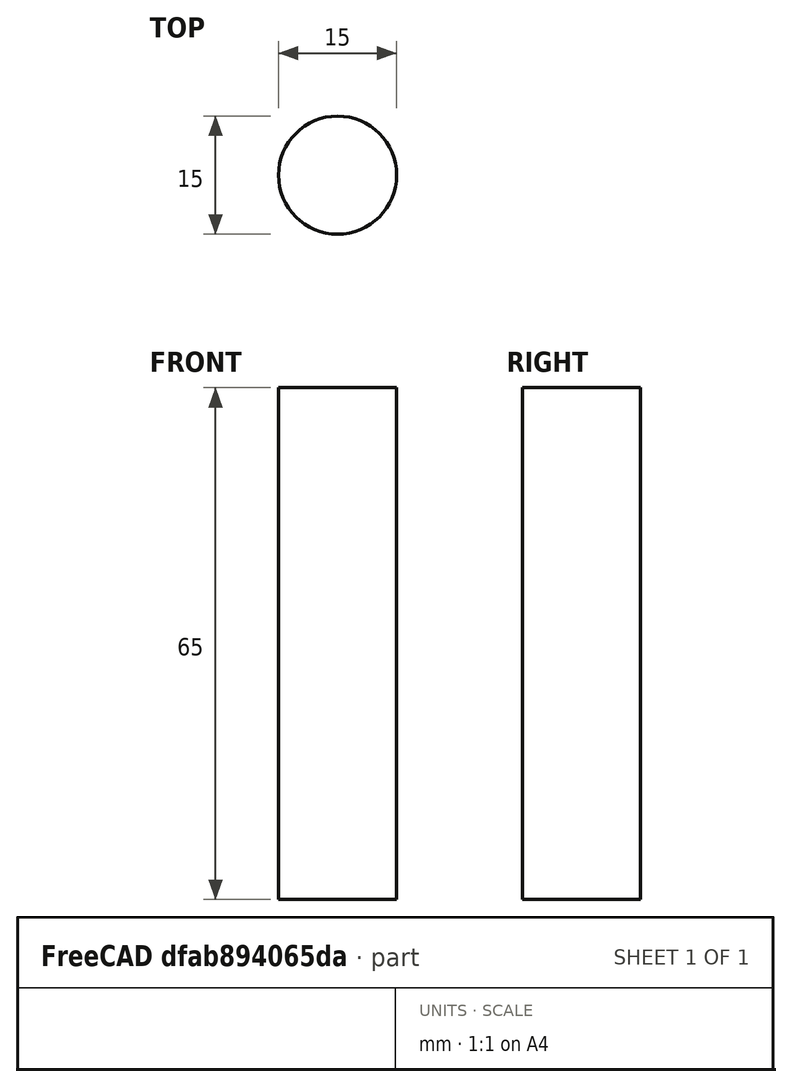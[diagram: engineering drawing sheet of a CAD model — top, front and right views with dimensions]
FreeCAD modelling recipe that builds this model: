
FCSTD DOCUMENT  (FreeCAD 0.18R4 (GitTag))
Label: baseAxle
License: All rights reserved
LicenseURL: http://en.wikipedia.org/wiki/All_rights_reserved
objects: Sketcher::SketchObject×1, PartDesign::Pad×1, PartDesign::Body×1, App::Part×1, Part::Feature×1
note: 5 computed .brp shape members not serialized (recipe doc carries the construction recipe); baked Part::Feature solids carry a one-line shape summary decoded from their .brp

FEATURE [Sketcher::SketchObject] Sketch
  MapMode = 5
  Support = -> [XY_Plane001]
  sketch-geometry (1):
    g0: Circle CenterX=0 CenterY=0 CenterZ=0 NormalX=0 NormalY=0 NormalZ=1 AngleXU=0 Radius=7.5
  constraints (2):
    c: Coincident(g0,g-1)
    c: Diameter(g0) = 15
FEATURE [PartDesign::Pad] Pad
  Length = 65
  Length2 = 100
  Profile = -> Sketch
  Type = 0
FEATURE [PartDesign::Body] Body  label="baseAxle"
  Group = -> [Sketch,Pad]
  Origin = -> Origin001
  Tip = -> Pad
FEATURE [App::Part] Part
  Group = -> [Body]
  Origin = -> Origin
FEATURE [Part::Feature] Pad001  label="Robot_BaseAxle"
  shape: bbox 15 x 15 x 65 mm, 3 faces (baked)
